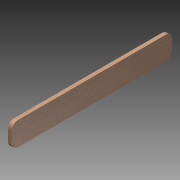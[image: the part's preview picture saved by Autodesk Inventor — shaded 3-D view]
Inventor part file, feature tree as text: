
AUTODESK INVENTOR PART (.ipt)
format: ipt  version: 2013 (Build 170138000, 138)  size: 90,624 bytes
history: native  units: in
note: dims shown in document units (in); Inventor stores cm internally (conversion verified against a paired STEP export)
features: extrude x1, fillet x1, sketch x1
ambient origin geometry x8: Origin, YZ Plane, XZ Plane, XY Plane, X Axis, Y Axis, Z Axis, Center Point
bodies: Solid1 (feature_tree)
feature tree (3):
  extrude  "Extrusion1"  Depth=0.75in
  fillet  "Fillet1"  Radius=34.0in
  sketch  "Sketch1"  dims[d0=5.0in d1=0.75in d2=34.0in d3=0.0in d4=1.3125in]
